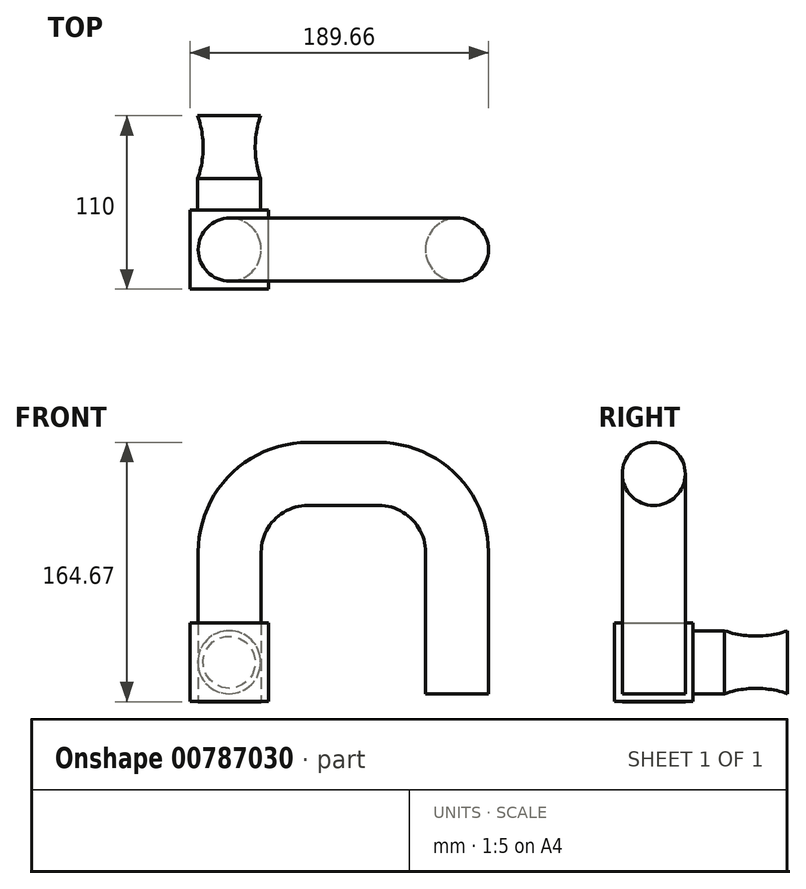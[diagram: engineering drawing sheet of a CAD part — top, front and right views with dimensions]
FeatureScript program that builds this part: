
annotation { "Feature Type Name" : "Feature", "Feature Type Description" : "" }
export const myFeature = defineFeature(function(context is Context, id is Id, definition is map)
    precondition{}
    {
        {
            var Q0;
            Q0=qCreatedBy(makeId("Front.planeOp"),FACE);
            var sketch = newSketch(context, id + "F0", { "sketchPlane" : qUnion([Q0])});
            skLineSegment(sketch, "E0", {"start": v(-40.9, 4.73) * mm, "end": v(-40.9, -35.27) * mm});
            skLineSegment(sketch, "E1", {"start": v(-40.9, -35.27) * mm, "end": v(14.1, -35.27) * mm});
            skLineSegment(sketch, "E2", {"start": v(14.1, 4.73) * mm, "end": v(-40.9, 4.73) * mm});
            skLineSegment(sketch, "E3", {"start": v(14.1, 4.73) * mm, "end": v(14.1, 64.73) * mm});
            skLineSegment(sketch, "E4", {"start": v(14.1, 64.73) * mm, "end": v(-15.9, 64.73) * mm});
            skLineSegment(sketch, "E5", {"start": v(-15.9, 64.73) * mm, "end": v(-40.9, 4.73) * mm});
            skLineSegment(sketch, "E6", {"start": v(14.1, 4.73) * mm, "end": v(14.1, -35.27) * mm});
            skLineSegment(sketch, "E7", {"start": v(14.1, -35.27) * mm, "end": v(14.1, 64.73) * mm});
            skPoint(sketch, "E8.end.orphan", {"position": v(69.1, 4.73) * mm});
            skPoint(sketch, "E9.orphan", {"position": v(69.1, -35.27) * mm});
            skLineSegment(sketch, "E10", {"start": v(14.1, -35.27) * mm, "end": v(-40.9, -35.27) * mm});
            skLineSegment(sketch, "E11", {"start": v(14.1, -15.27) * mm, "end": v(14.1, 74.73) * mm});
            skLineSegment(sketch, "E12", {"start": v(-35.9, 124.73) * mm, "end": v(-80.9, 124.73) * mm});
            skLineSegment(sketch, "E13", {"start": v(-130.9, 74.73) * mm, "end": v(-130.9, -20.27) * mm});
            skPoint(sketch, "E14.visualSharp", {"position": v(14.1, 124.73) * mm});
            skArc(sketch, "E14.filletArc", {"start": v(14.1, 74.73) * mm, "mid": v(-0.55, 110.09) * mm, "end": v(-35.9, 124.73) * mm});
            skPoint(sketch, "E15.visualSharp", {"position": v(-130.9, 124.73) * mm});
            skArc(sketch, "E15.filletArc", {"start": v(-80.9, 124.73) * mm, "mid": v(-116.26, 110.09) * mm, "end": v(-130.9, 74.73) * mm});
            skLineSegment(sketch, "E16", {"start": v(-130.9, -20.27) * mm, "end": v(-112.51, -20.27) * mm});
            skLineSegment(sketch, "E17", {"start": v(-112.51, -20.27) * mm, "end": v(-161.77, -20.27) * mm});
            skSolve(sketch);
        }
        {
            var Q0;
            Q0=qCreatedBy(makeId("Front.planeOp"),FACE);
            var sketch = newSketch(context, id + "F1", { "sketchPlane" : qUnion([Q0])});
            skLineSegment(sketch, "E18", {"start": v(-40.9, -35.27) * mm, "end": v(-40.9, 4.8) * mm});
            skLineSegment(sketch, "E19", {"start": v(69.1, 4.73) * mm, "end": v(69.1, -35.27) * mm});
            skLineSegment(sketch, "E20.0.0", {"start": v(69.1, -35.27) * mm, "end": v(-40.9, -35.27) * mm});
            skLineSegment(sketch, "E21.0", {"start": v(14.1, -35.27) * mm, "end": v(-40.9, -35.27) * mm});
            skPoint(sketch, "E22.start.orphan", {"position": v(14.1, -35.27) * mm});
            skPoint(sketch, "E23.end.orphan", {"position": v(-40.9, -35.27) * mm});
            skLineSegment(sketch, "E24.bottom", {"start": v(-155.9, 29.8) * mm, "end": v(-105.9, 29.8) * mm});
            skLineSegment(sketch, "E24.top", {"start": v(-155.9, -20.2) * mm, "end": v(-105.9, -20.2) * mm});
            skLineSegment(sketch, "E24.left", {"start": v(-155.9, 29.8) * mm, "end": v(-155.9, -20.2) * mm});
            skLineSegment(sketch, "E24.right", {"start": v(-105.9, 29.8) * mm, "end": v(-105.9, -20.2) * mm});
            skPoint(sketch, "E24.middle", {"position": v(-130.9, 4.8) * mm});
            skSolve(sketch);
        }
        {
            var Q0;
            {var subQ0=sQuery(id+"F1.wireOp",EDGE,"E24.bottom");Q0=makeQuery(id+"F1.imprint","IMPRINT",FACE,{"disambiguationData":[TD([[makeQuery(id+"F1.imprint","IMPRINT",EDGE,{"derivedFrom":subQ0}),-1.0]])]});}
            extrude(context, id + "F2", {"entities" : qUnion([Q0]), "depth" : 25 * mm, "offsetDistance" : 25 * mm, "hasSecondDirection" : true, "secondDirectionOppositeDirection" : true, "secondDirectionDepth" : 25 * mm});
        }
        {
            var Q0;
            Q0=makeQuery(id+"F2.opExtrude","SWEPT_FACE",FACE,{"disambiguationData":[OSD([sQuery(id+"F1.wireOp",EDGE,"E24.top")])]});
            var sketch = newSketch(context, id + "F3", { "sketchPlane" : qUnion([Q0])});
            skCircle(sketch, "E25", {"center": v(-130.57, 0) * mm, "radius": 20 * mm});
            skSolve(sketch);
        }
        {
            var Q0;
            Q0=makeQuery(id+"F3.imprint","IMPRINT",FACE,{"disambiguationData":[TD([[makeQuery(id+"F3.imprint","IMPRINT",EDGE,{"derivedFrom":sQuery(id+"F3.wireOp",EDGE,"E25")}),1.0]])]});
            var Q1;
            Q1=sQuery(id+"F0.wireOp",EDGE,"E13");
            var Q2;
            Q2=sQuery(id+"F0.wireOp",EDGE,"E15.filletArc");
            var Q3;
            Q3=sQuery(id+"F0.wireOp",EDGE,"E12");
            var Q4;
            Q4=sQuery(id+"F0.wireOp",EDGE,"E14.filletArc");
            var Q5;
            Q5=sQuery(id+"F0.wireOp",EDGE,"E11");
            sweep(context, id + "F4", {"profiles" : qUnion([Q0]), "path" : qUnion([Q1, Q2, Q3, Q4, Q5])});
        }
        {
            var Q0;
            Q0=makeQuery(id+"F2.opExtrude","CAP_FACE",FACE,{"disambiguationData":[OSD([sQuery(id+"F1.wireOp",EDGE,"E24.bottom"),sQuery(id+"F1.wireOp",EDGE,"E24.top"),sQuery(id+"F1.wireOp",EDGE,"E24.left"),sQuery(id+"F1.wireOp",EDGE,"E24.right")])],"isStart":true});
            var sketch = newSketch(context, id + "F5", { "sketchPlane" : qUnion([Q0])});
            skCircle(sketch, "E26", {"center": v(130.9, 4.8) * mm, "radius": 20 * mm});
            skPoint(sketch, "E26.centerSnap0", {"position": v(130.9, 29.8) * mm});
            skPoint(sketch, "E26.centerSnap1", {"position": v(155.9, 4.8) * mm});
            skSolve(sketch);
        }
        {
            var Q0;
            Q0=makeQuery(id+"F5.imprint","IMPRINT",FACE,{"disambiguationData":[TD([[makeQuery(id+"F5.imprint","IMPRINT",EDGE,{"derivedFrom":sQuery(id+"F5.wireOp",EDGE,"E26")}),1.0]])]});
            extrude(context, id + "F6", {"entities" : qUnion([Q0]), "operationType" : NewBodyOperationType.ADD, "depth" : 60 * mm, "offsetDistance" : 25 * mm});
        }
        {
            var Q0;
            Q0=makeQuery(id+"F2.opExtrude","SWEPT_FACE",FACE,{"disambiguationData":[OSD([sQuery(id+"F1.wireOp",EDGE,"E24.left")])]});
            cPlane(context, id + "F7", {"entities" : qUnion([Q0]), "cplaneType" : CPlaneType.OFFSET, "offset" : 25 * mm, "oppositeDirection" : true, "width" : 150 * mm, "height" : 150 * mm});
        }
        {
            var Q0;
            Q0=qCreatedBy(id+"F7.planeOp",FACE);
            var sketch = newSketch(context, id + "F8", { "sketchPlane" : qUnion([Q0])});
            skLineSegment(sketch, "E27.0", {"start": v(-85, -15.2) * mm, "end": v(-85, 24.8) * mm});
            skLineSegment(sketch, "E28", {"start": v(-85, 4.8) * mm, "end": v(-117.63, 4.8) * mm});
            skLineSegment(sketch, "E29", {"start": v(-85, 24.8) * mm, "end": v(-45, 24.8) * mm});
            skArc(sketch, "E30", {"start": v(-85, 24.8) * mm, "mid": v(-65, 21.37) * mm, "end": v(-45, 24.8) * mm});
            skSolve(sketch);
        }
        {
            var Q0;
            Q0 = qSketchRegion(id + "F8", true);
            var Q1;
            Q1=makeQuery(id+"F6.opExtrude","CAP_EDGE",EDGE,{"disambiguationData":[OSD([sQuery(id+"F5.wireOp",EDGE,"E26")])],"isStart":false});
            revolve(context, id + "F9", {"operationType" : NewBodyOperationType.REMOVE, "surfaceOperationType" : NewSurfaceOperationType.NEW, "entities" : qUnion([Q0]), "axis" : qUnion([Q1]), "revolveType" : RevolveType.FULL});
        }
    });
